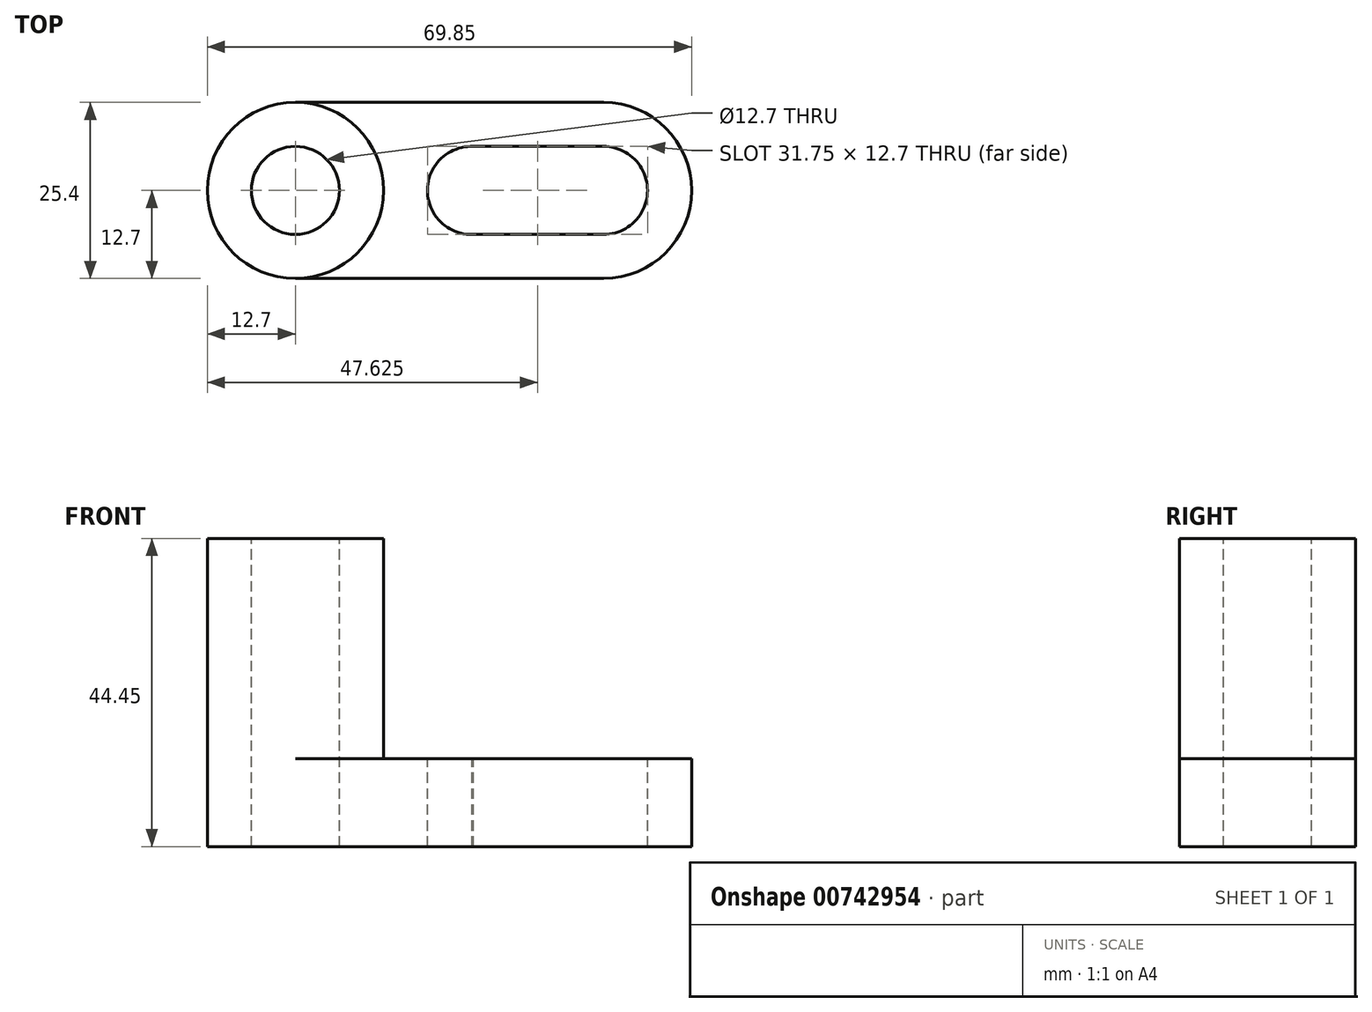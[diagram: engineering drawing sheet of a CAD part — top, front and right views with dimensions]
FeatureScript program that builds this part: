
annotation { "Feature Type Name" : "Feature", "Feature Type Description" : "" }
export const myFeature = defineFeature(function(context is Context, id is Id, definition is map)
    precondition{}
    {
        {
            var Q0;
            Q0=qCreatedBy(makeId("Front.planeOp"),FACE);
            var sketch = newSketch(context, id + "F0", { "sketchPlane" : qUnion([Q0])});
            skLineSegment(sketch, "E0.bottom", {"start": v(0, 0) * mm, "end": v(69.85, 0) * mm});
            skLineSegment(sketch, "E0.top", {"start": v(0, 44.45) * mm, "end": v(69.85, 44.45) * mm});
            skLineSegment(sketch, "E0.left", {"start": v(0, 0) * mm, "end": v(0, 44.45) * mm});
            skLineSegment(sketch, "E0.right", {"start": v(69.85, 0) * mm, "end": v(69.85, 44.45) * mm});
            skSolve(sketch);
        }
        {
            var Q0;
            Q0 = qSketchRegion(id + "F0", true);
            extrude(context, id + "F1", {"entities" : qUnion([Q0]), "depth" : 25.4 * mm, "offsetDistance" : 25.4 * mm});
        }
        {
            var Q0;
            Q0=makeQuery(id+"F1.opExtrude","CAP_FACE",FACE,{"disambiguationData":[OSD([sQuery(id+"F0.wireOp",EDGE,"E0.bottom"),sQuery(id+"F0.wireOp",EDGE,"E0.top"),sQuery(id+"F0.wireOp",EDGE,"E0.left"),sQuery(id+"F0.wireOp",EDGE,"E0.right")])],"isStart":false});
            var sketch = newSketch(context, id + "F2", { "sketchPlane" : qUnion([Q0])});
            skLineSegment(sketch, "E1.bottom", {"start": v(69.85, 44.45) * mm, "end": v(25.4, 44.45) * mm});
            skLineSegment(sketch, "E1.top", {"start": v(69.85, 12.7) * mm, "end": v(25.4, 12.7) * mm});
            skLineSegment(sketch, "E1.left", {"start": v(69.85, 44.45) * mm, "end": v(69.85, 12.7) * mm});
            skLineSegment(sketch, "E1.right", {"start": v(25.4, 44.45) * mm, "end": v(25.4, 12.7) * mm});
            skSolve(sketch);
        }
        {
            var Q0;
            Q0 = qSketchRegion(id + "F2", true);
            extrude(context, id + "F3", {"entities" : qUnion([Q0]), "operationType" : NewBodyOperationType.REMOVE, "oppositeDirection" : true, "depth" : 25.4 * mm, "offsetDistance" : 25.4 * mm});
        }
        {
            var Q0;
            Q0=makeQuery(id+"F1.opExtrude","SWEPT_FACE",FACE,{"disambiguationData":[OSD([sQuery(id+"F0.wireOp",EDGE,"E0.top")])]});
            var sketch = newSketch(context, id + "F4", { "sketchPlane" : qUnion([Q0])});
            skArc(sketch, "E2", {"start": v(12.7, 0) * mm, "mid": v(3.72, -3.72) * mm, "end": v(0, -12.7) * mm});
            skLineSegment(sketch, "E3", {"start": v(12.7, 0) * mm, "end": v(0, 0) * mm});
            skLineSegment(sketch, "E4", {"start": v(0, 0) * mm, "end": v(0, -12.7) * mm});
            skSolve(sketch);
        }
        {
            var Q0;
            Q0 = qSketchRegion(id + "F4", true);
            extrude(context, id + "F5", {"entities" : qUnion([Q0]), "operationType" : NewBodyOperationType.REMOVE, "oppositeDirection" : true, "depth" : 50.8 * mm, "offsetDistance" : 25.4 * mm});
        }
        {
            var Q0;
            Q0=makeQuery(id+"F1.opExtrude","SWEPT_FACE",FACE,{"disambiguationData":[OSD([sQuery(id+"F0.wireOp",EDGE,"E0.top")])]});
            var sketch = newSketch(context, id + "F6", { "sketchPlane" : qUnion([Q0])});
            skArc(sketch, "E5", {"start": v(0, -12.7) * mm, "mid": v(3.72, -21.68) * mm, "end": v(12.7, -25.4) * mm});
            skLineSegment(sketch, "E6", {"start": v(12.7, -25.4) * mm, "end": v(0, -25.4) * mm});
            skLineSegment(sketch, "E7", {"start": v(0, -25.4) * mm, "end": v(0, -12.7) * mm});
            skSolve(sketch);
        }
        {
            var Q0;
            Q0 = qSketchRegion(id + "F6", true);
            extrude(context, id + "F7", {"entities" : qUnion([Q0]), "operationType" : NewBodyOperationType.REMOVE, "oppositeDirection" : true, "depth" : 50.8 * mm, "offsetDistance" : 25.4 * mm});
        }
        {
            var Q0;
            Q0=makeQuery(id+"F1.opExtrude","SWEPT_FACE",FACE,{"disambiguationData":[OSD([sQuery(id+"F0.wireOp",EDGE,"E0.top")])]});
            var sketch = newSketch(context, id + "F8", { "sketchPlane" : qUnion([Q0])});
            skArc(sketch, "E8", {"start": v(12.7, -25.4) * mm, "mid": v(21.68, -21.68) * mm, "end": v(25.4, -12.7) * mm});
            skLineSegment(sketch, "E9", {"start": v(12.7, -25.4) * mm, "end": v(25.4, -25.4) * mm});
            skLineSegment(sketch, "E10", {"start": v(25.4, -25.4) * mm, "end": v(25.4, -12.7) * mm});
            skSolve(sketch);
        }
        {
            var Q0;
            Q0 = qSketchRegion(id + "F8", true);
            extrude(context, id + "F9", {"entities" : qUnion([Q0]), "operationType" : NewBodyOperationType.REMOVE, "oppositeDirection" : true, "depth" : 31.75 * mm, "offsetDistance" : 25.4 * mm});
        }
        {
            var Q0;
            Q0=makeQuery(id+"F1.opExtrude","SWEPT_FACE",FACE,{"disambiguationData":[OSD([sQuery(id+"F0.wireOp",EDGE,"E0.top")])]});
            var sketch = newSketch(context, id + "F10", { "sketchPlane" : qUnion([Q0])});
            skArc(sketch, "E11", {"start": v(25.4, -12.7) * mm, "mid": v(21.68, -3.72) * mm, "end": v(12.7, 0) * mm});
            skLineSegment(sketch, "E12", {"start": v(12.7, 0) * mm, "end": v(25.4, 0) * mm});
            skLineSegment(sketch, "E13", {"start": v(25.4, 0) * mm, "end": v(25.4, -12.7) * mm});
            skSolve(sketch);
        }
        {
            var Q0;
            Q0 = qSketchRegion(id + "F10", true);
            extrude(context, id + "F11", {"entities" : qUnion([Q0]), "operationType" : NewBodyOperationType.REMOVE, "oppositeDirection" : true, "depth" : 31.75 * mm, "offsetDistance" : 25.4 * mm});
        }
        {
            var Q0;
            Q0=makeQuery(id+"F11.boolean.opBoolean","MERGE",FACE,{"derivedFrom":[makeQuery(id+"F9.boolean.opBoolean","MERGE",FACE,{"derivedFrom":[makeQuery(id+"F3.boolean.opBoolean","COPY",FACE,{"derivedFrom":makeQuery(id+"F3.opExtrude","SWEPT_FACE",FACE,{"disambiguationData":[OSD([sQuery(id+"F2.wireOp",EDGE,"E1.top")])]})}),makeQuery(id+"F9.opExtrude","CAP_FACE",FACE,{"disambiguationData":[OSD([sQuery(id+"F8.wireOp",EDGE,"E8"),sQuery(id+"F8.wireOp",EDGE,"E9"),sQuery(id+"F8.wireOp",EDGE,"E10")])],"isStart":false})]}),makeQuery(id+"F11.opExtrude","CAP_FACE",FACE,{"disambiguationData":[OSD([sQuery(id+"F10.wireOp",EDGE,"E11"),sQuery(id+"F10.wireOp",EDGE,"E12"),sQuery(id+"F10.wireOp",EDGE,"E13")])],"isStart":false})]});
            var sketch = newSketch(context, id + "F12", { "sketchPlane" : qUnion([Q0])});
            skCircle(sketch, "E14", {"center": v(57.15, -12.7) * mm, "radius": 6.35 * mm});
            skCircle(sketch, "E15", {"center": v(38.1, -12.7) * mm, "radius": 6.35 * mm});
            skLineSegment(sketch, "E16", {"start": v(37.98, -19.05) * mm, "end": v(57.15, -19.05) * mm});
            skLineSegment(sketch, "E17", {"start": v(37.81, -6.36) * mm, "end": v(57.15, -6.35) * mm});
            skSolve(sketch);
        }
        {
            var Q0;
            Q0 = qSketchRegion(id + "F12", true);
            extrude(context, id + "F13", {"entities" : qUnion([Q0]), "operationType" : NewBodyOperationType.REMOVE, "oppositeDirection" : true, "depth" : 25.4 * mm, "offsetDistance" : 25.4 * mm});
        }
        {
            var Q0;
            Q0=makeQuery(id+"F1.opExtrude","SWEPT_FACE",FACE,{"disambiguationData":[OSD([sQuery(id+"F0.wireOp",EDGE,"E0.top")])]});
            var sketch = newSketch(context, id + "F14", { "sketchPlane" : qUnion([Q0])});
            skCircle(sketch, "E18", {"center": v(12.7, -12.7) * mm, "radius": 6.35 * mm});
            skSolve(sketch);
        }
        {
            var Q0;
            Q0 = qSketchRegion(id + "F14", true);
            extrude(context, id + "F15", {"entities" : qUnion([Q0]), "operationType" : NewBodyOperationType.REMOVE, "oppositeDirection" : true, "depth" : 50.8 * mm, "offsetDistance" : 25.4 * mm});
        }
        {
            var Q0;
            Q0=makeQuery(id+"F11.boolean.opBoolean","MERGE",FACE,{"derivedFrom":[makeQuery(id+"F9.boolean.opBoolean","MERGE",FACE,{"derivedFrom":[makeQuery(id+"F3.boolean.opBoolean","COPY",FACE,{"derivedFrom":makeQuery(id+"F3.opExtrude","SWEPT_FACE",FACE,{"disambiguationData":[OSD([sQuery(id+"F2.wireOp",EDGE,"E1.top")])]})}),makeQuery(id+"F9.opExtrude","CAP_FACE",FACE,{"disambiguationData":[OSD([sQuery(id+"F8.wireOp",EDGE,"E8"),sQuery(id+"F8.wireOp",EDGE,"E9"),sQuery(id+"F8.wireOp",EDGE,"E10")])],"isStart":false})]}),makeQuery(id+"F11.opExtrude","CAP_FACE",FACE,{"disambiguationData":[OSD([sQuery(id+"F10.wireOp",EDGE,"E11"),sQuery(id+"F10.wireOp",EDGE,"E12"),sQuery(id+"F10.wireOp",EDGE,"E13")])],"isStart":false})]});
            var sketch = newSketch(context, id + "F16", { "sketchPlane" : qUnion([Q0])});
            skArc(sketch, "E19", {"start": v(69.85, -12.7) * mm, "mid": v(66.13, -3.72) * mm, "end": v(57.15, 0) * mm});
            skArc(sketch, "E20", {"start": v(57.15, -25.4) * mm, "mid": v(66.13, -21.68) * mm, "end": v(69.85, -12.7) * mm});
            skLineSegment(sketch, "E21", {"start": v(57.15, 0) * mm, "end": v(69.85, 0) * mm});
            skLineSegment(sketch, "E22", {"start": v(69.85, 0) * mm, "end": v(69.85, -12.7) * mm});
            skLineSegment(sketch, "E23", {"start": v(69.85, -25.4) * mm, "end": v(57.15, -25.4) * mm});
            skLineSegment(sketch, "E24", {"start": v(69.85, -25.4) * mm, "end": v(69.85, -12.7) * mm});
            skSolve(sketch);
        }
        {
            var Q0;
            Q0 = qSketchRegion(id + "F16", true);
            extrude(context, id + "F17", {"entities" : qUnion([Q0]), "operationType" : NewBodyOperationType.REMOVE, "oppositeDirection" : true, "depth" : 25.4 * mm, "offsetDistance" : 25.4 * mm});
        }
    });
